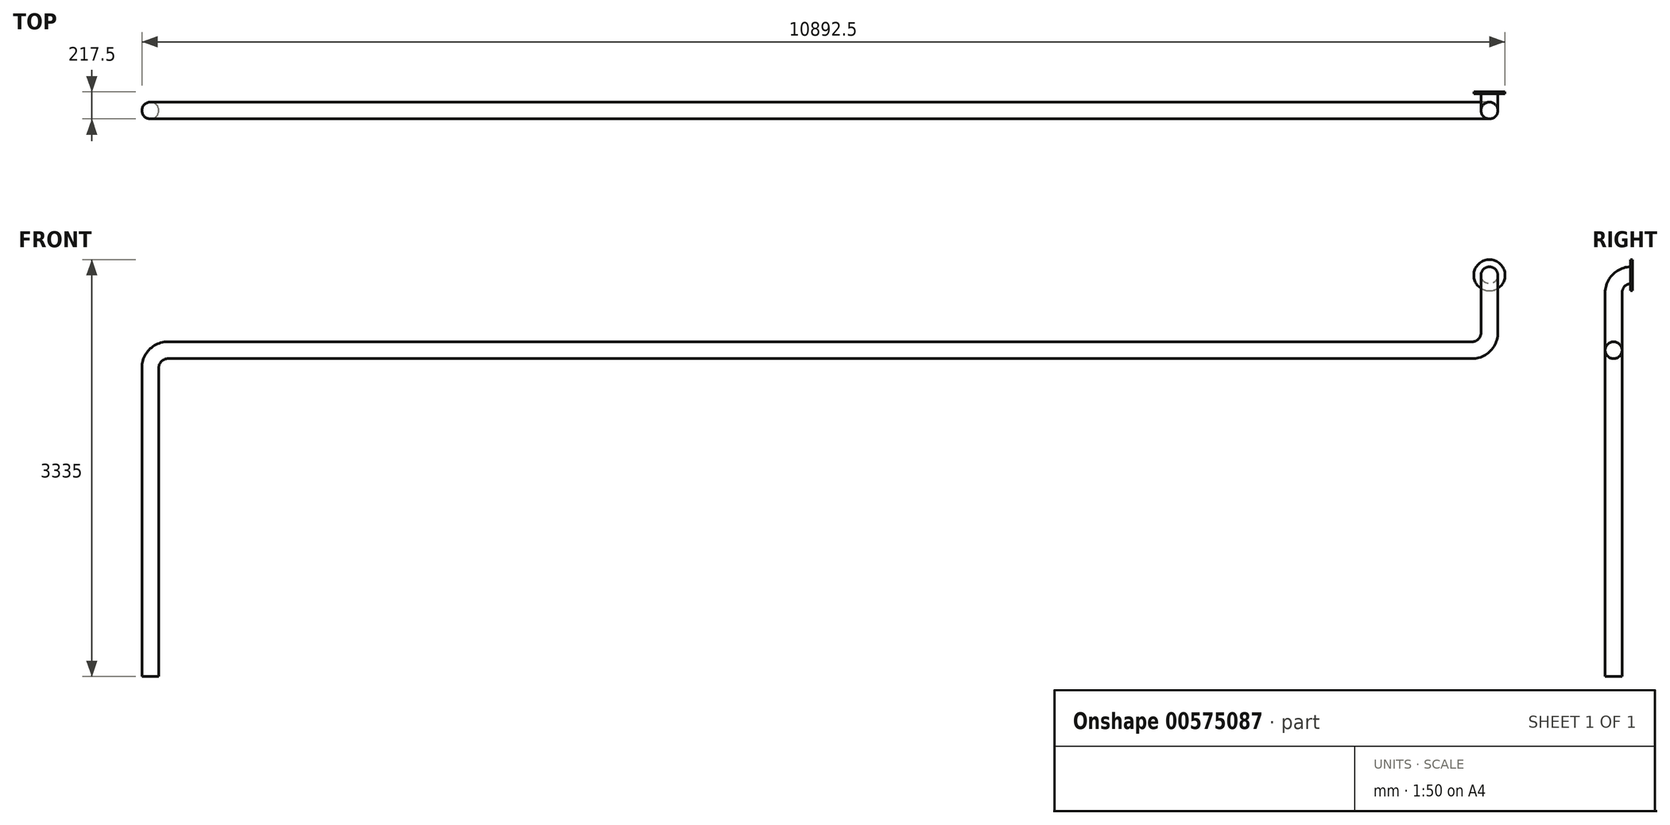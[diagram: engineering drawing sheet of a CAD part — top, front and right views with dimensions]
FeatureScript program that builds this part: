
annotation { "Feature Type Name" : "Feature", "Feature Type Description" : "" }
export const myFeature = defineFeature(function(context is Context, id is Id, definition is map)
    precondition{}
    {
        {
            var Q0;
            Q0=qCreatedBy(makeId("Front.planeOp"),FACE);
            var sketch = newSketch(context, id + "F0", { "sketchPlane" : qUnion([Q0])});
            skCircle(sketch, "E0", {"center": v(0, 0) * mm, "radius": 67.5 * mm});
            skCircle(sketch, "E1", {"center": v(0, 0) * mm, "radius": 125 * mm});
            skSolve(sketch);
        }
        {
            var Q0;
            Q0=qCreatedBy(makeId("Right.planeOp"),FACE);
            var sketch = newSketch(context, id + "F1", { "sketchPlane" : qUnion([Q0])});
            skLineSegment(sketch, "E2", {"start": v(0, 0) * mm, "end": v(-10, 0) * mm});
            skLineSegment(sketch, "E3", {"start": v(-150, -140) * mm, "end": v(-150, -600) * mm});
            skPoint(sketch, "E4.visualSharp", {"position": v(-150, 0) * mm});
            skArc(sketch, "E4.filletArc", {"start": v(-10, 0) * mm, "mid": v(-109, -41) * mm, "end": v(-150, -140) * mm});
            skSolve(sketch);
        }
        {
            var Q0;
            Q0=qCreatedBy(makeId("Front.planeOp"),FACE);
            cPlane(context, id + "F2", {"entities" : qUnion([Q0]), "cplaneType" : CPlaneType.OFFSET, "offset" : 150 * mm, "width" : 150 * mm, "height" : 150 * mm});
        }
        {
            var Q0;
            Q0=qCreatedBy(id+"F2.planeOp",FACE);
            var sketch = newSketch(context, id + "F3", { "sketchPlane" : qUnion([Q0])});
            skLineSegment(sketch, "E5.0", {"start": v(0, -140) * mm, "end": v(0, -460) * mm});
            skLineSegment(sketch, "E6", {"start": v(-140, -600) * mm, "end": v(-10560, -600) * mm});
            skLineSegment(sketch, "E7", {"start": v(-10700, -740) * mm, "end": v(-10700, -3210) * mm});
            skPoint(sketch, "E8.visualSharp", {"position": v(-10700, -600) * mm});
            skArc(sketch, "E8.filletArc", {"start": v(-10560, -600) * mm, "mid": v(-10659, -641) * mm, "end": v(-10700, -740) * mm});
            skPoint(sketch, "E9.visualSharp", {"position": v(0, -600) * mm});
            skArc(sketch, "E9.filletArc", {"start": v(-140, -600) * mm, "mid": v(-41, -559) * mm, "end": v(0, -460) * mm});
            skSolve(sketch);
        }
        {
            var Q0;
            Q0=makeQuery(id+"F0.imprint","IMPRINT",FACE,{"disambiguationData":[TD([[makeQuery(id+"F0.imprint","IMPRINT",EDGE,{"derivedFrom":sQuery(id+"F0.wireOp",EDGE,"E0")}),1.0]])]});
            var Q1;
            Q1=sQuery(id+"F1.wireOp",EDGE,"E2");
            var Q2;
            Q2=sQuery(id+"F1.wireOp",EDGE,"E4.filletArc");
            var Q3;
            Q3=sQuery(id+"F3.wireOp",EDGE,"E5.0");
            var Q4;
            Q4=sQuery(id+"F3.wireOp",EDGE,"E9.filletArc");
            var Q5;
            Q5=sQuery(id+"F3.wireOp",EDGE,"E6");
            var Q6;
            Q6=sQuery(id+"F3.wireOp",EDGE,"E8.filletArc");
            var Q7;
            Q7=sQuery(id+"F3.wireOp",EDGE,"E7");
            sweep(context, id + "F4", {"profiles" : qUnion([Q0]), "path" : qUnion([Q1, Q2, Q3, Q4, Q5, Q6, Q7])});
        }
        {
            var Q0;
            Q0=makeQuery(id+"F0.imprint","IMPRINT",FACE,{"disambiguationData":[TD([[makeQuery(id+"F0.imprint","IMPRINT",EDGE,{"derivedFrom":sQuery(id+"F0.wireOp",EDGE,"E0")}),-1.0]])]});
            extrude(context, id + "F5", {"entities" : qUnion([Q0]), "operationType" : NewBodyOperationType.ADD, "depth" : 15 * mm, "offsetDistance" : 25 * mm});
        }
    });
